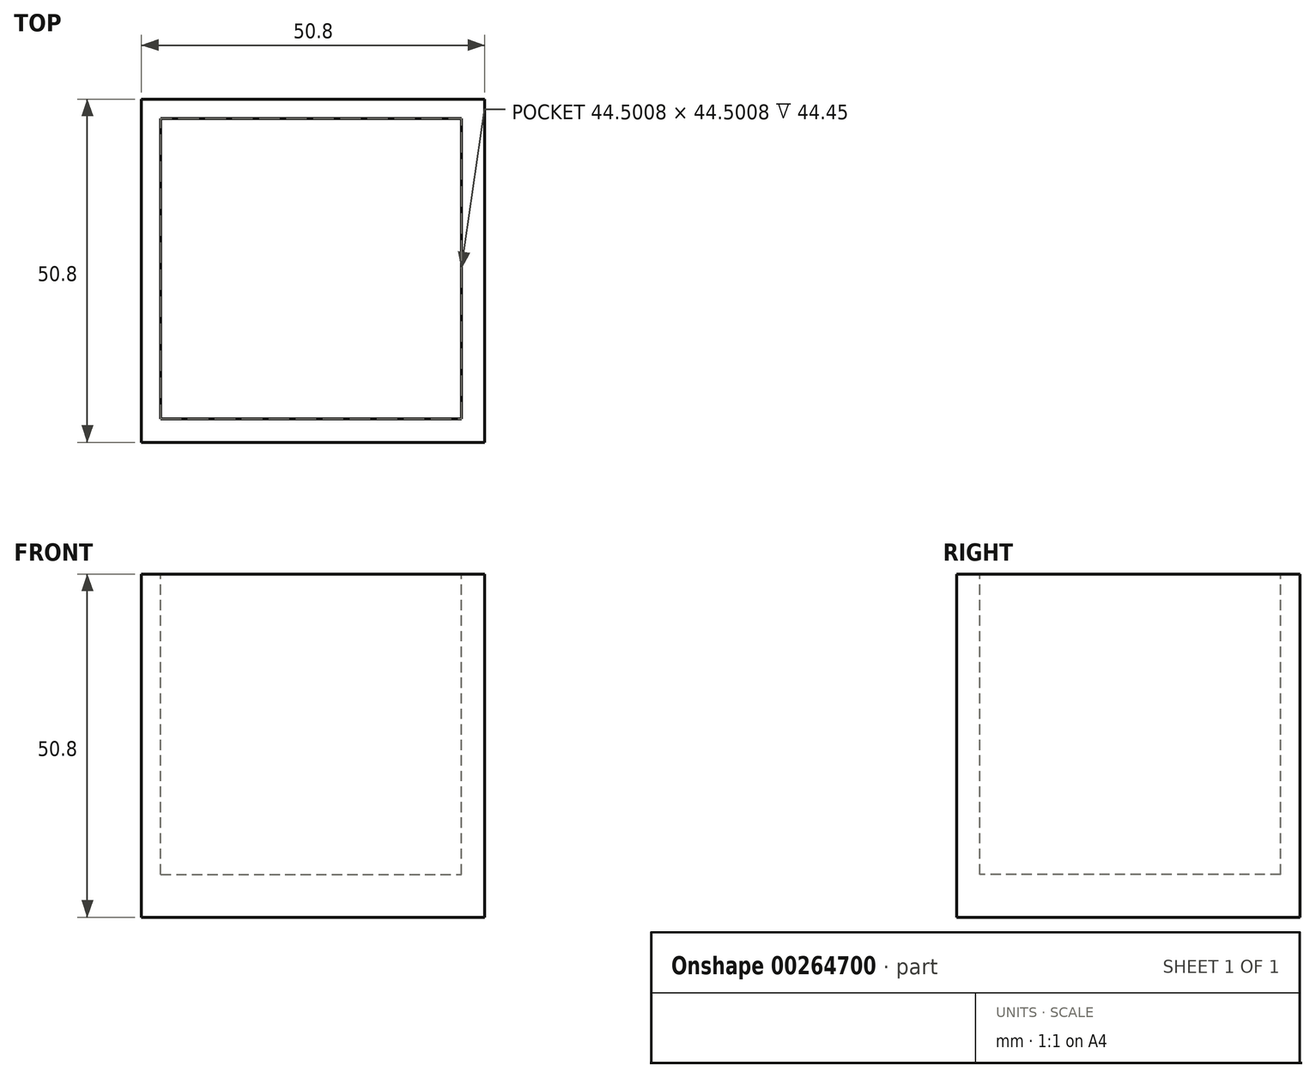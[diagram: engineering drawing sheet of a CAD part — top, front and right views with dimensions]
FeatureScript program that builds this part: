
annotation { "Feature Type Name" : "Feature", "Feature Type Description" : "" }
export const myFeature = defineFeature(function(context is Context, id is Id, definition is map)
    precondition{}
    {
        {
            var Q0;
            Q0=qCreatedBy(makeId("Front.planeOp"),FACE);
            var sketch = newSketch(context, id + "F0", { "sketchPlane" : qUnion([Q0])});
            skLineSegment(sketch, "E0.bottom", {"start": v(0, 0) * mm, "end": v(-50.8, 0) * mm});
            skLineSegment(sketch, "E0.top", {"start": v(0, 50.8) * mm, "end": v(-50.8, 50.8) * mm});
            skLineSegment(sketch, "E0.left", {"start": v(0, 0) * mm, "end": v(0, 50.8) * mm});
            skLineSegment(sketch, "E0.right", {"start": v(-50.8, 0) * mm, "end": v(-50.8, 50.8) * mm});
            skSolve(sketch);
        }
        {
            var Q0;
            Q0 = qSketchRegion(id + "F0", true);
            extrude(context, id + "F1", {"entities" : qUnion([Q0]), "depth" : 50.8 * mm});
        }
        {
            var Q0;
            Q0=makeQuery(id+"F1.opExtrude","SWEPT_FACE",FACE,{"disambiguationData":[OSD([sQuery(id+"F0.wireOp",EDGE,"E0.top")])]});
            var sketch = newSketch(context, id + "F2", { "sketchPlane" : qUnion([Q0])});
            skLineSegment(sketch, "E1.bottom", {"start": v(-47.94, -2.86) * mm, "end": v(-3.44, -2.86) * mm});
            skLineSegment(sketch, "E1.top", {"start": v(-47.94, -47.36) * mm, "end": v(-3.44, -47.36) * mm});
            skLineSegment(sketch, "E1.left", {"start": v(-47.94, -2.86) * mm, "end": v(-47.94, -47.36) * mm});
            skLineSegment(sketch, "E1.right", {"start": v(-3.44, -2.86) * mm, "end": v(-3.44, -47.36) * mm});
            skSolve(sketch);
        }
        {
            var Q0;
            Q0=makeQuery(id+"F2.imprint","IMPRINT",FACE,{"disambiguationData":[TD([[makeQuery(id+"F2.imprint","IMPRINT",EDGE,{"derivedFrom":sQuery(id+"F2.wireOp",EDGE,"E1.bottom")}),-1.0]])]});
            var sketch = newSketch(context, id + "F3", { "sketchPlane" : qUnion([Q0])});
            skSolve(sketch);
        }
        {
            var Q0;
            Q0 = qSketchRegion(id + "F3", true);
            var Q1;
            Q1=makeQuery(id+"F2.imprint","IMPRINT",FACE,{"disambiguationData":[TD([[makeQuery(id+"F2.imprint","IMPRINT",EDGE,{"derivedFrom":sQuery(id+"F2.wireOp",EDGE,"E1.bottom")}),-1.0]])]});
            extrude(context, id + "F4", {"entities" : qUnion([Q0, Q1]), "operationType" : NewBodyOperationType.REMOVE, "oppositeDirection" : true, "depth" : 44.45 * mm});
        }
    });
